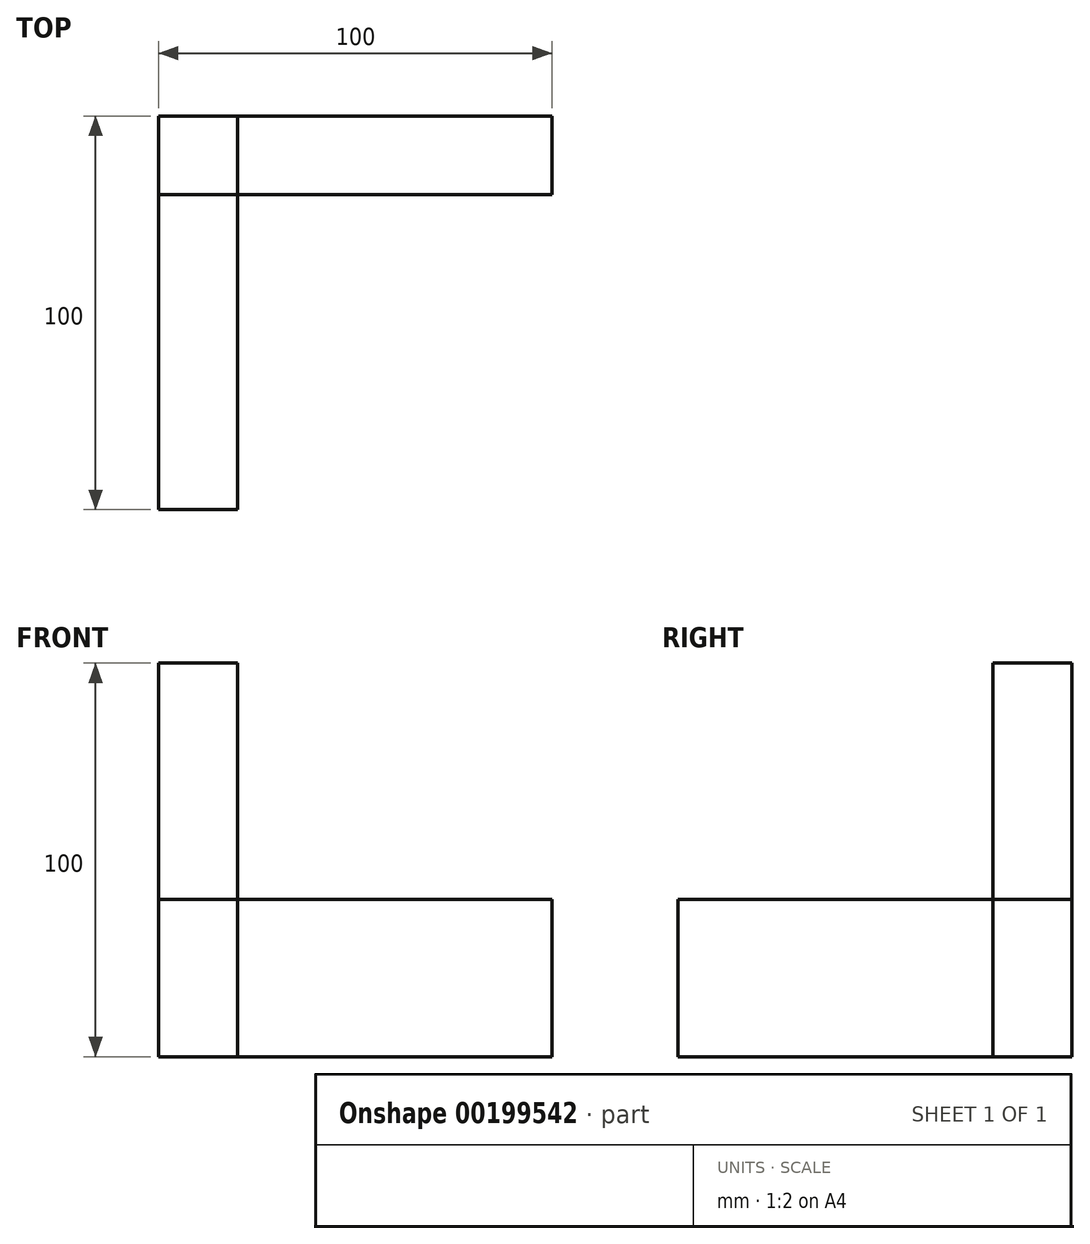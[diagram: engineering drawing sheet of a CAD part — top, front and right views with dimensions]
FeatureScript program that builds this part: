
annotation { "Feature Type Name" : "Feature", "Feature Type Description" : "" }
export const myFeature = defineFeature(function(context is Context, id is Id, definition is map)
    precondition{}
    {
        {
            var Q0;
            Q0=qCreatedBy(makeId("Top.planeOp"),FACE);
            var sketch = newSketch(context, id + "F0", { "sketchPlane" : qUnion([Q0])});
            skLineSegment(sketch, "E0.bottom", {"start": v(50, 50) * mm, "end": v(-50, 50) * mm});
            skLineSegment(sketch, "E0.top", {"start": v(50, -50) * mm, "end": v(-50, -50) * mm});
            skLineSegment(sketch, "E0.left", {"start": v(50, 50) * mm, "end": v(50, -50) * mm});
            skLineSegment(sketch, "E0.right", {"start": v(-50, 50) * mm, "end": v(-50, -50) * mm});
            skPoint(sketch, "E0.middle", {"position": v(0, 0) * mm});
            skSolve(sketch);
        }
        {
            var Q0;
            Q0 = qSketchRegion(id + "F0", true);
            extrude(context, id + "F1", {"entities" : qUnion([Q0]), "depth" : 15 * mm});
        }
        {
            var Q0;
            Q0=makeQuery(id+"F1.opExtrude","CAP_FACE",FACE,{"disambiguationData":[OSD([sQuery(id+"F0.wireOp",EDGE,"E0.bottom"),sQuery(id+"F0.wireOp",EDGE,"E0.top"),sQuery(id+"F0.wireOp",EDGE,"E0.left"),sQuery(id+"F0.wireOp",EDGE,"E0.right")])],"isStart":false});
            var sketch = newSketch(context, id + "F2", { "sketchPlane" : qUnion([Q0])});
            skLineSegment(sketch, "E1", {"start": v(-50, 50) * mm, "end": v(-30, 50) * mm, "construction": true});
            skLineSegment(sketch, "E2", {"start": v(-30, 50) * mm, "end": v(-30, 30) * mm, "construction": true});
            skLineSegment(sketch, "E3", {"start": v(-30, 30) * mm, "end": v(50, 30) * mm});
            skLineSegment(sketch, "E4", {"start": v(-30, 30) * mm, "end": v(-30, -50) * mm});
            skLineSegment(sketch, "E5", {"start": v(-30, -50) * mm, "end": v(-50, -50) * mm});
            skLineSegment(sketch, "E6", {"start": v(-50, -50) * mm, "end": v(-50, 50) * mm});
            skLineSegment(sketch, "E7", {"start": v(-50, 50) * mm, "end": v(50, 50) * mm});
            skLineSegment(sketch, "E8", {"start": v(50, 30) * mm, "end": v(50, 50) * mm});
            skSolve(sketch);
        }
        {
            var Q0;
            Q0=makeQuery(id+"F2.imprint","IMPRINT",FACE,{"disambiguationData":[TD([[makeQuery(id+"F2.imprint","IMPRINT",EDGE,{"derivedFrom":sQuery(id+"F2.wireOp",EDGE,"E3")}),1.0]])]});
            extrude(context, id + "F3", {"entities" : qUnion([Q0]), "operationType" : NewBodyOperationType.ADD, "depth" : 25 * mm});
        }
        {
            var Q0;
            Q0=makeQuery(id+"F1.opExtrude","CAP_FACE",FACE,{"disambiguationData":[OSD([sQuery(id+"F0.wireOp",EDGE,"E0.bottom"),sQuery(id+"F0.wireOp",EDGE,"E0.top"),sQuery(id+"F0.wireOp",EDGE,"E0.left"),sQuery(id+"F0.wireOp",EDGE,"E0.right")])],"isStart":false});
            var sketch = newSketch(context, id + "F4", { "sketchPlane" : qUnion([Q0])});
            skLineSegment(sketch, "E9", {"start": v(-30, -10) * mm, "end": v(50, -10) * mm, "construction": true});
            skLineSegment(sketch, "E10", {"start": v(10, 30) * mm, "end": v(10, -50) * mm, "construction": true});
            skCircle(sketch, "E11", {"center": v(10, -10) * mm, "radius": 30 * mm});
            skSolve(sketch);
        }
        {
            var Q0;
            Q0=makeQuery(id+"F4.imprint","IMPRINT",FACE,{"disambiguationData":[TD([[makeQuery(id+"F4.imprint","IMPRINT",EDGE,{"derivedFrom":sQuery(id+"F4.wireOp",EDGE,"E11")}),1.0]])]});
            extrude(context, id + "F5", {"entities" : qUnion([Q0]), "operationType" : NewBodyOperationType.REMOVE, "endBound" : BoundingType.THROUGH_ALL, "oppositeDirection" : true, "depth" : 25 * mm});
        }
        {
            var Q0;
            Q0=makeQuery(id+"F3.opExtrude","CAP_FACE",FACE,{"disambiguationData":[OSD([sQuery(id+"F2.wireOp",EDGE,"E3"),sQuery(id+"F2.wireOp",EDGE,"E4"),sQuery(id+"F2.wireOp",EDGE,"E5"),sQuery(id+"F2.wireOp",EDGE,"E6"),sQuery(id+"F2.wireOp",EDGE,"E7"),sQuery(id+"F2.wireOp",EDGE,"E8")])],"isStart":false});
            var sketch = newSketch(context, id + "F6", { "sketchPlane" : qUnion([Q0])});
            skLineSegment(sketch, "E12.bottom", {"start": v(-50, 50) * mm, "end": v(-30, 50) * mm});
            skLineSegment(sketch, "E12.top", {"start": v(-50, 30) * mm, "end": v(-30, 30) * mm});
            skLineSegment(sketch, "E12.left", {"start": v(-50, 50) * mm, "end": v(-50, 30) * mm});
            skLineSegment(sketch, "E12.right", {"start": v(-30, 50) * mm, "end": v(-30, 30) * mm});
            skSolve(sketch);
        }
        {
            var Q0;
            Q0 = qSketchRegion(id + "F6", true);
            extrude(context, id + "F7", {"entities" : qUnion([Q0]), "operationType" : NewBodyOperationType.ADD, "depth" : 60 * mm});
        }
        {
            var Q0;
            Q0=makeQuery(id+"F1.opExtrude","CAP_FACE",FACE,{"disambiguationData":[OSD([sQuery(id+"F0.wireOp",EDGE,"E0.bottom"),sQuery(id+"F0.wireOp",EDGE,"E0.top"),sQuery(id+"F0.wireOp",EDGE,"E0.left"),sQuery(id+"F0.wireOp",EDGE,"E0.right")])],"isStart":false});
            var sketch = newSketch(context, id + "F8", { "sketchPlane" : qUnion([Q0])});
            skLineSegment(sketch, "E13.bottom", {"start": v(-30, 30) * mm, "end": v(50, 30) * mm});
            skLineSegment(sketch, "E13.top", {"start": v(-30, -50) * mm, "end": v(50, -50) * mm});
            skLineSegment(sketch, "E13.left", {"start": v(-30, 30) * mm, "end": v(-30, -50) * mm});
            skLineSegment(sketch, "E13.right", {"start": v(50, 30) * mm, "end": v(50, -50) * mm});
            skSolve(sketch);
        }
        {
            var Q0;
            Q0 = qSketchRegion(id + "F8", true);
            extrude(context, id + "F9", {"entities" : qUnion([Q0]), "operationType" : NewBodyOperationType.REMOVE, "endBound" : BoundingType.THROUGH_ALL, "oppositeDirection" : true, "depth" : 25 * mm});
        }
    });
